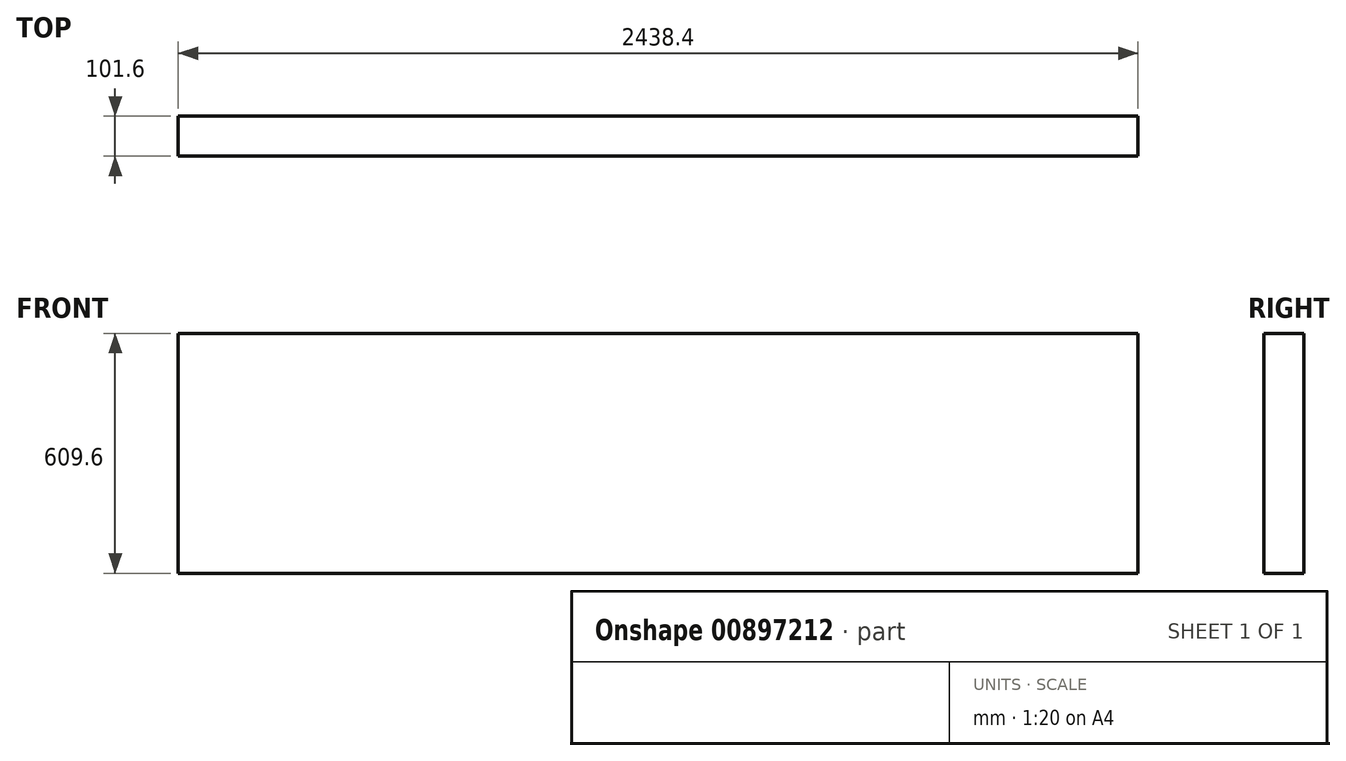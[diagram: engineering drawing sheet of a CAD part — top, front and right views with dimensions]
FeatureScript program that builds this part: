
annotation { "Feature Type Name" : "Feature", "Feature Type Description" : "" }
export const myFeature = defineFeature(function(context is Context, id is Id, definition is map)
    precondition{}
    {
        {
            var Q0;
            Q0=qCreatedBy(makeId("Front.planeOp"),FACE);
            var sketch = newSketch(context, id + "F0", { "sketchPlane" : qUnion([Q0])});
            skLineSegment(sketch, "E0.bottom", {"start": v(0, 0) * mm, "end": v(2438.4, 0) * mm});
            skLineSegment(sketch, "E0.top", {"start": v(0, 609.6) * mm, "end": v(2438.4, 609.6) * mm});
            skLineSegment(sketch, "E0.left", {"start": v(0, 0) * mm, "end": v(0, 609.6) * mm});
            skLineSegment(sketch, "E0.right", {"start": v(2438.4, 0) * mm, "end": v(2438.4, 609.6) * mm});
            skLineSegment(sketch, "E1", {"start": v(1219.2, 747.3) * mm, "end": v(1219.2, -798.54) * mm, "construction": true});
            skPoint(sketch, "E1.startSnap0", {"position": v(1219.2, 609.6) * mm});
            skSolve(sketch);
        }
        {
            var Q0;
            Q0=qSketchRegion(id+"F0",true);
            extrude(context, id + "F1", {"entities" : qUnion([Q0]), "depth" : 101.6 * mm, "offsetDistance" : 25.4 * mm});
        }
    });
